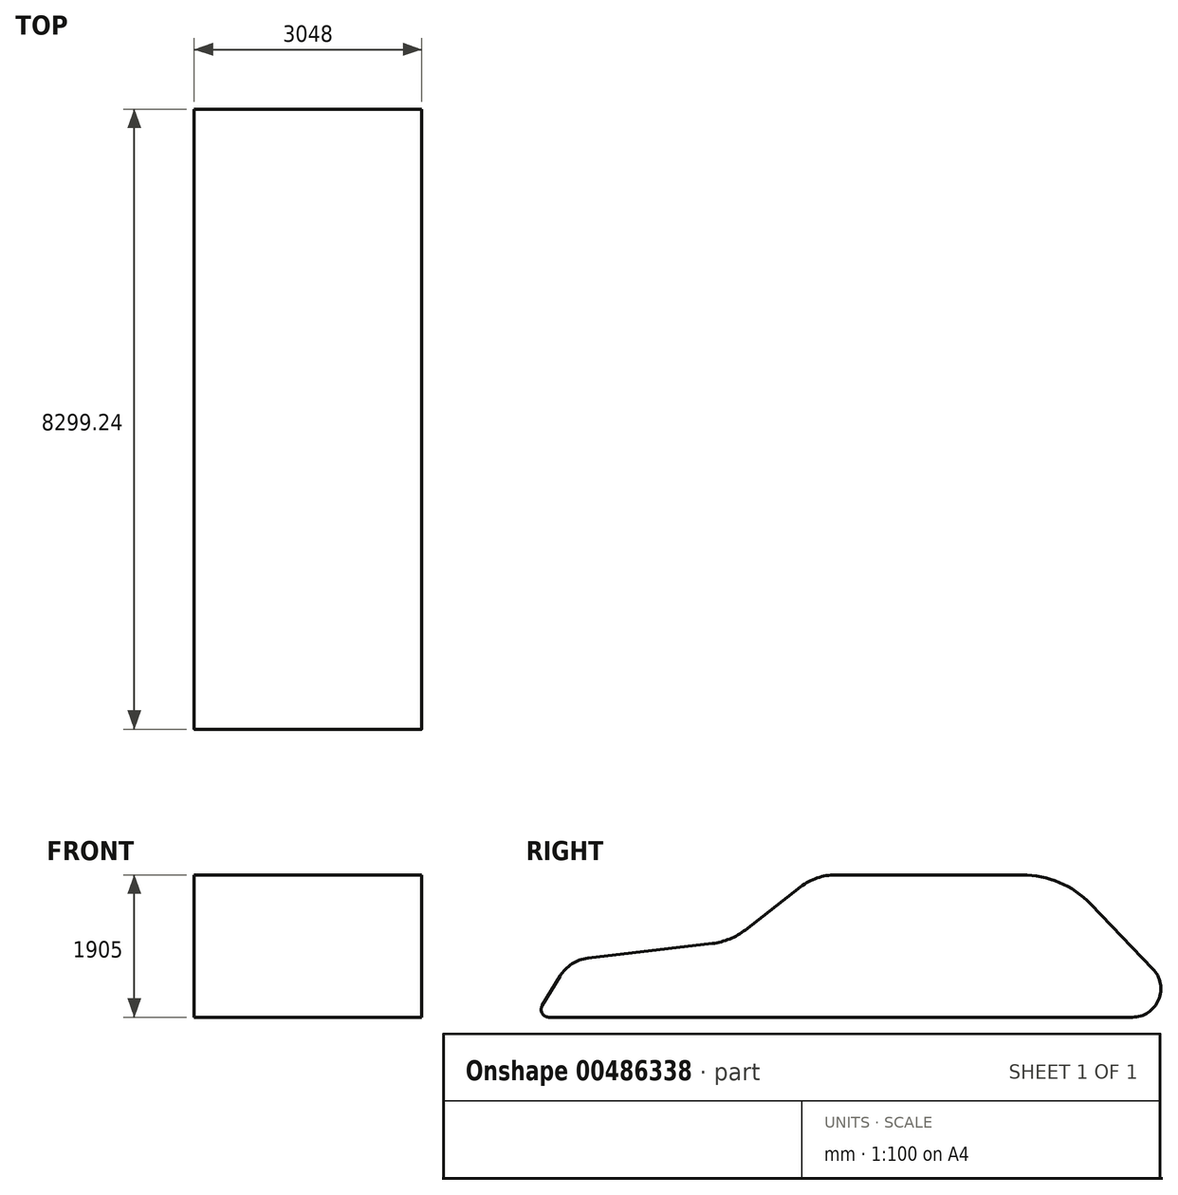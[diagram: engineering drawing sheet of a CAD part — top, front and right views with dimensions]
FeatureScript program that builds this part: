
annotation { "Feature Type Name" : "Feature", "Feature Type Description" : "" }
export const myFeature = defineFeature(function(context is Context, id is Id, definition is map)
    precondition{}
    {
        {
            var Q0;
            Q0=qCreatedBy(makeId("Right.planeOp"),FACE);
            var sketch = newSketch(context, id + "F0", { "sketchPlane" : qUnion([Q0])});
            skLineSegment(sketch, "E0", {"start": v(-3542.24, -109.38) * mm, "end": v(4274.4, -109.38) * mm});
            skLineSegment(sketch, "E1", {"start": v(-3629.36, 44.5) * mm, "end": v(-3392.89, 438.62) * mm});
            skPoint(sketch, "E2.visualSharp", {"position": v(-3721.69, -109.38) * mm});
            skArc(sketch, "E2.filletArc", {"start": v(-3629.36, 44.5) * mm, "mid": v(-3630.66, -57.84) * mm, "end": v(-3542.24, -109.38) * mm});
            skLineSegment(sketch, "E3", {"start": v(-3016.64, 681.78) * mm, "end": v(-1351.71, 877.65) * mm});
            skPoint(sketch, "E4.visualSharp", {"position": v(-3264.49, 652.62) * mm});
            skArc(sketch, "E4.filletArc", {"start": v(-3016.64, 681.78) * mm, "mid": v(-3233.01, 603.91) * mm, "end": v(-3392.89, 438.62) * mm});
            skLineSegment(sketch, "E5", {"start": v(-909.8, 1058.83) * mm, "end": v(-168.86, 1635.1) * mm});
            skPoint(sketch, "E6.visualSharp", {"position": v(-1105.49, 906.62) * mm});
            skArc(sketch, "E6.filletArc", {"start": v(-1351.71, 877.65) * mm, "mid": v(-1118.36, 938) * mm, "end": v(-909.8, 1058.83) * mm});
            skLineSegment(sketch, "E7", {"start": v(298.96, 1795.62) * mm, "end": v(2798.22, 1795.62) * mm});
            skLineSegment(sketch, "E8", {"start": v(3714.38, 1405.13) * mm, "end": v(4549.25, 535.47) * mm});
            skPoint(sketch, "E9.visualSharp", {"position": v(5168.31, -109.38) * mm});
            skArc(sketch, "E9.filletArc", {"start": v(4274.4, -109.38) * mm, "mid": v(4624.9, 122.23) * mm, "end": v(4549.25, 535.47) * mm});
            skPoint(sketch, "E10.visualSharp", {"position": v(3339.51, 1795.62) * mm});
            skArc(sketch, "E10.filletArc", {"start": v(3714.38, 1405.13) * mm, "mid": v(3296.17, 1693.93) * mm, "end": v(2798.22, 1795.62) * mm});
            skPoint(sketch, "E11.visualSharp", {"position": v(37.51, 1795.62) * mm});
            skArc(sketch, "E11.filletArc", {"start": v(298.96, 1795.62) * mm, "mid": v(51.66, 1754.37) * mm, "end": v(-168.86, 1635.1) * mm});
            skSolve(sketch);
        }
        {
            var Q0;
            Q0=makeQuery(id+"F0.imprint","IMPRINT",FACE,{"disambiguationData":[TD([[makeQuery(id+"F0.imprint","IMPRINT",EDGE,{"derivedFrom":sQuery(id+"F0.wireOp",EDGE,"E0")}),1.0]])]});
            extrude(context, id + "F1", {"entities" : qUnion([Q0]), "oppositeDirection" : true, "depth" : 3048 * mm});
        }
    });
